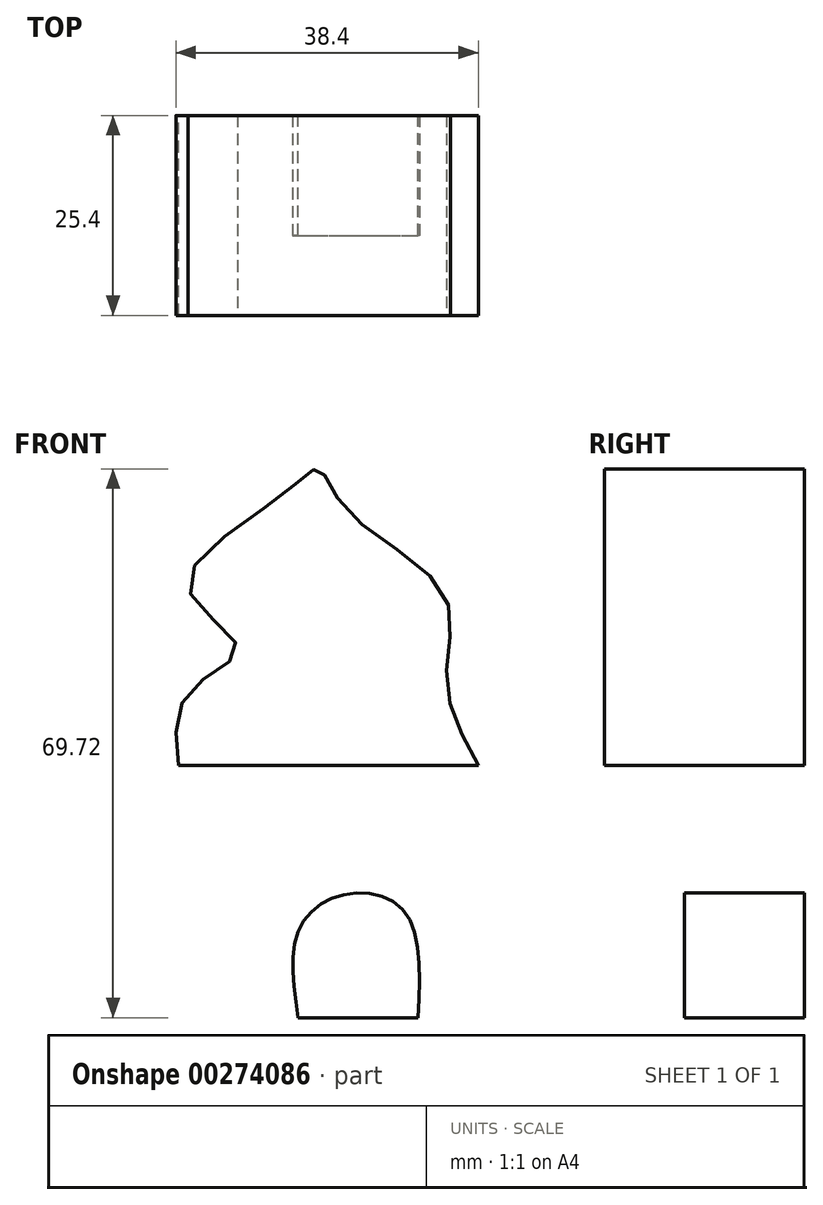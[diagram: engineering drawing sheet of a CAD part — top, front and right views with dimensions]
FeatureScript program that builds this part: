
annotation { "Feature Type Name" : "Feature", "Feature Type Description" : "" }
export const myFeature = defineFeature(function(context is Context, id is Id, definition is map)
    precondition{}
    {
        {
            var Q0;
            Q0=qCreatedBy(makeId("Front.planeOp"),FACE);
            var sketch = newSketch(context, id + "F0", { "sketchPlane" : qUnion([Q0])});
            skLineSegment(sketch, "E0", {"start": v(-21.2, 7.74) * mm, "end": v(16.9, 7.74) * mm});
            skFitSpline(sketch, "E1", {"points": [v(-21.2, 7.74) * mm, v(-19.77, 17.15) * mm, v(-13.69, 22.68) * mm, v(-19.91, 30.42) * mm, v(-8.02, 42.03) * mm, v(-3.32, 45.35) * mm, v(0, 40.37) * mm, v(12.58, 29.45) * mm, v(12.86, 18.53) * mm, v(16.9, 7.74) * mm], "startDerivative": vector(-10.69, 97.52) * mm, "endDerivative": vector(49.8, -89.23) * mm});
            skPoint(sketch, "E2", {"position": v(-11, 13.17) * mm});
            skSolve(sketch);
        }
        {
            var Q0;
            Q0 = qSketchRegion(id + "F0", true);
            extrude(context, id + "F1", {"entities" : qUnion([Q0]), "depth" : 25.4 * mm});
        }
        {
            var Q0;
            Q0=qCreatedBy(makeId("Front.planeOp"),FACE);
            var sketch = newSketch(context, id + "F2", { "sketchPlane" : qUnion([Q0])});
            skLineSegment(sketch, "E3", {"start": v(-5.96, -24.33) * mm, "end": v(9.28, -24.33) * mm});
            skFitSpline(sketch, "E4", {"points": [v(-5.96, -24.33) * mm, v(-5.96, -13.27) * mm, v(0, -8.66) * mm, v(7.56, -10.88) * mm, v(9.28, -24.33) * mm], "startDerivative": vector(-6.98, 46.03) * mm, "endDerivative": vector(-2.59, -54.61) * mm});
            skSolve(sketch);
        }
        {
            var Q0;
            Q0=makeQuery(id+"F2.imprint","IMPRINT",FACE,{"disambiguationData":[TD([[makeQuery(id+"F2.imprint","IMPRINT",EDGE,{"derivedFrom":sQuery(id+"F2.wireOp",EDGE,"E3")}),1.0]])]});
            extrude(context, id + "F3", {"entities" : qUnion([Q0]), "depth" : 15.24 * mm});
        }
        {
            var Q0;
            Q0=makeQuery(id+"F1.opExtrude","CAP_FACE",FACE,{"disambiguationData":[OSD([sQuery(id+"F0.wireOp",EDGE,"E0"),sQuery(id+"F0.wireOp",EDGE,"E1")])],"isStart":false});
            var sketch = newSketch(context, id + "F4", { "sketchPlane" : qUnion([Q0])});
            skCircle(sketch, "E5", {"center": v(7.55, 13.65) * mm, "radius": 5.5 * mm});
            skPoint(sketch, "E6", {"position": v(7.55, 11.62) * mm});
            skSolve(sketch);
        }
    });
